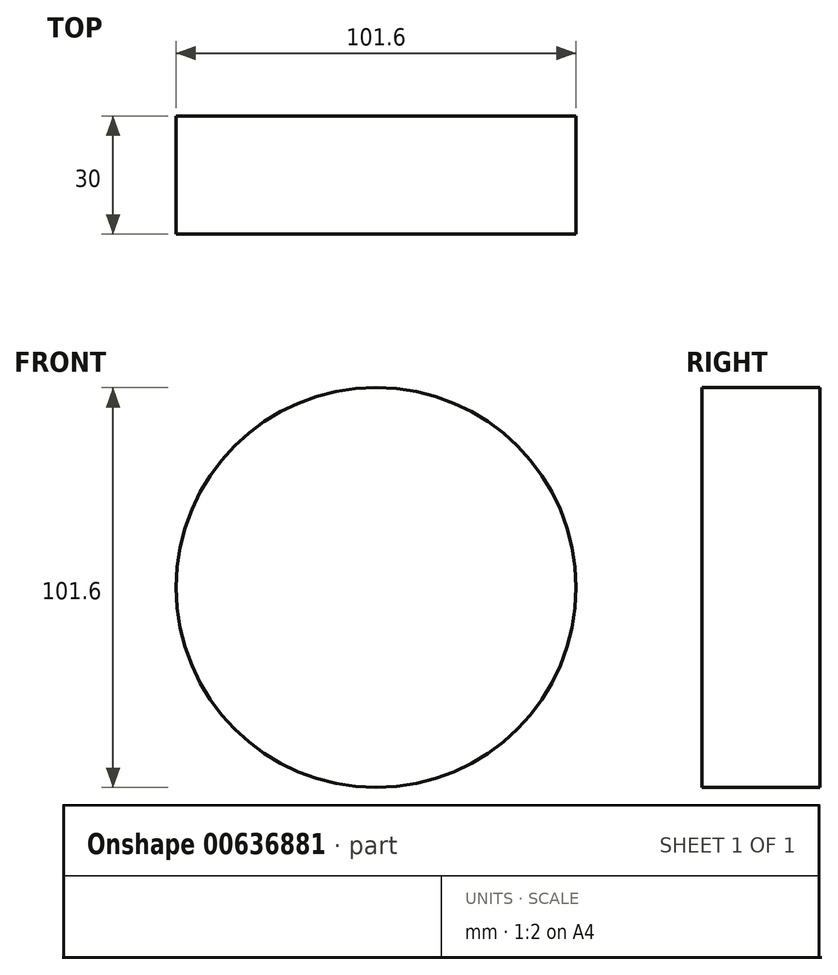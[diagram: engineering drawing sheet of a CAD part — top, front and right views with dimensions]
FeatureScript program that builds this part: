
annotation { "Feature Type Name" : "Feature", "Feature Type Description" : "" }
export const myFeature = defineFeature(function(context is Context, id is Id, definition is map)
    precondition{}
    {
        {
            var Q0;
            Q0=qCreatedBy(makeId("Front.planeOp"),FACE);
            var sketch = newSketch(context, id + "F0", { "sketchPlane" : qUnion([Q0])});
            skCircle(sketch, "E0", {"center": v(0, 0) * mm, "radius": 50.8 * mm});
            skSolve(sketch);
        }
        {
            var Q0;
            Q0 = qSketchRegion(id + "F0", true);
            var Q1;
            Q1=makeQuery(id+"F0.imprint","IMPRINT",FACE,{"disambiguationData":[TD([[makeQuery(id+"F0.imprint","IMPRINT",EDGE,{"derivedFrom":sQuery(id+"F0.wireOp",EDGE,"E0")}),1.0]])]});
            extrude(context, id + "F1", {"entities" : qUnion([Q0, Q1]), "depth" : 30 * mm, "offsetDistance" : 25.4 * mm});
        }
    });
